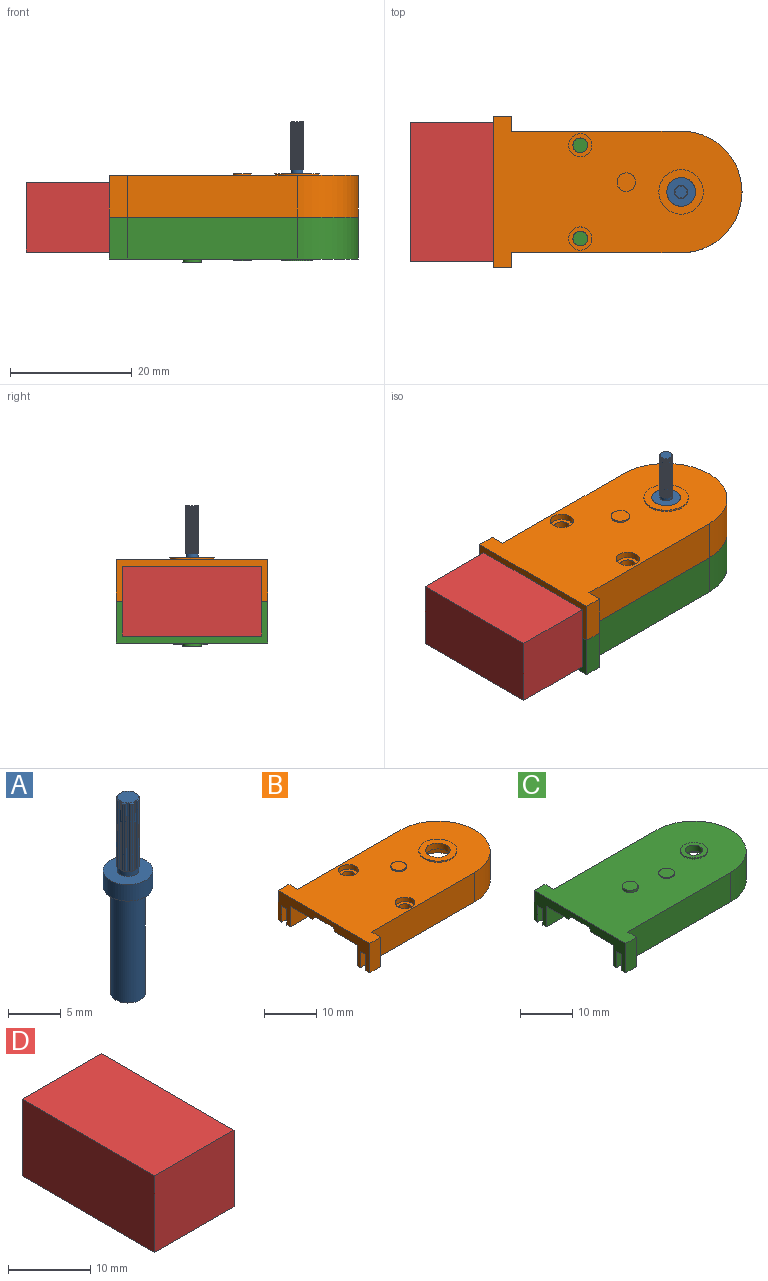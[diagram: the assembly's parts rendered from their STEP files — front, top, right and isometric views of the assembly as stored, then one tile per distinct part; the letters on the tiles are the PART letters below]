
ASSEMBLY  parts=4 mates=3
PART A: 79 faces, bbox 4.7x4.7x22.7 mm
  f0: plane 4.7x4.7mm, normal (0,0,-1), area 8.8mm2, adj f76,f77
  f1: plane 0.48x0.29mm, normal (0,0,-1), area 0mm2, adj f21,f22,f23,f24,f73
  f2: plane 0.48x0.29mm, normal (0,0,-1), area 0mm2, adj f25,f26,f27,f28,f73
  f3: plane 0.48x0.29mm, normal (0,0,-1), area 0mm2, adj f29,f30,f31,f32,f73
  f4: plane 0.48x0.29mm, normal (0,0,-1), area 0mm2, adj f33,f34,f35,f36,f73
  f5: plane 0.48x0.29mm, normal (0,0,-1), area 0mm2, adj f37,f38,f39,f40,f73
  f6: plane 0.48x0.29mm, normal (0,0,-1), area 0mm2, adj f41,f42,f43,f44,f73
  f7: plane 0.48x0.29mm, normal (0,0,-1), area 0mm2, adj f45,f46,f47,f48,f73
  f8: plane 0.48x0.29mm, normal (0,0,-1), area 0mm2, adj f17,f18,f19,f20,f73
  f9: plane 7.87x0.13mm, normal (0.71,0.71,0), area 1.5mm2, adj f17,f48,f49,f74
  f10: plane 7.87x0.19mm, normal (1,0,0), area 1.5mm2, adj f20,f21,f49,f66
  f11: plane 7.87x0.13mm, normal (0.71,-0.71,0), area 1.5mm2, adj f24,f25,f49,f67
  f12: plane 7.87x0.19mm, normal (0,-1,0), area 1.5mm2, adj f28,f29,f49,f68
  f13: plane 7.87x0.13mm, normal (-0.71,-0.71,0), area 1.5mm2, adj f32,f33,f49,f69
  f14: plane 7.87x0.19mm, normal (-1,0,0), area 1.5mm2, adj f36,f37,f49,f70
  f15: plane 7.87x0.13mm, normal (-0.71,0.71,0), area 1.5mm2, adj f40,f41,f49,f71
  f16: plane 7.87x0.19mm, normal (0,1,0), area 1.5mm2, adj f44,f45,f49,f72
  f17: plane 7.87x0.19mm, normal (-0.07,1,0), area 1.5mm2, adj f8,f9,f18,f49,f57,f74
  f18: plane 7.75x0.19mm, normal (0.88,0.47,0), area 1.7mm2, adj f8,f17,f19,f57
  f19: plane 7.75x0.21mm, normal (0.96,0.29,0), area 1.7mm2, adj f8,f18,f20,f56
  f20: plane 7.87x0.14mm, normal (0.65,-0.76,0), area 1.5mm2, adj f8,f10,f19,f49,f56,f66
  f21: plane 7.87x0.14mm, normal (0.65,0.76,0), area 1.5mm2, adj f1,f10,f22,f49,f59,f66
  f22: plane 7.75x0.21mm, normal (0.96,-0.29,0), area 1.7mm2, adj f1,f21,f23,f59
  f23: plane 7.75x0.19mm, normal (0.88,-0.47,0), area 1.7mm2, adj f1,f22,f24,f58
  f24: plane 7.87x0.19mm, normal (-0.07,-1,0), area 1.5mm2, adj f1,f11,f23,f49,f58,f67
  f25: plane 7.87x0.19mm, normal (1,0.07,0), area 1.5mm2, adj f2,f11,f26,f49,f61,f67
  f26: plane 7.75x0.19mm, normal (0.47,-0.88,0), area 1.7mm2, adj f2,f25,f27,f61
  f27: plane 7.75x0.21mm, normal (0.29,-0.96,0), area 1.7mm2, adj f2,f26,f28,f60
  f28: plane 7.87x0.14mm, normal (-0.76,-0.65,0), area 1.5mm2, adj f2,f12,f27,f49,f60,f68
  f29: plane 7.87x0.14mm, normal (0.76,-0.65,0), area 1.5mm2, adj f3,f12,f30,f49,f63,f68
  f30: plane 7.75x0.21mm, normal (-0.29,-0.96,0), area 1.7mm2, adj f3,f29,f31,f63
  f31: plane 7.75x0.19mm, normal (-0.47,-0.88,0), area 1.7mm2, adj f3,f30,f32,f62
  f32: plane 7.87x0.19mm, normal (-1,0.07,0), area 1.5mm2, adj f3,f13,f31,f49,f62,f69
  f33: plane 7.87x0.19mm, normal (0.07,-1,0), area 1.5mm2, adj f4,f13,f34,f49,f64,f69
  f34: plane 7.75x0.19mm, normal (-0.88,-0.47,0), area 1.7mm2, adj f4,f33,f35,f64
  f35: plane 7.75x0.21mm, normal (-0.96,-0.29,0), area 1.7mm2, adj f4,f34,f36,f65
  f36: plane 7.87x0.14mm, normal (-0.65,0.76,0), area 1.5mm2, adj f4,f14,f35,f49,f65,f70
  f37: plane 7.87x0.14mm, normal (-0.65,-0.76,0), area 1.5mm2, adj f5,f14,f38,f49,f51,f70
  f38: plane 7.75x0.21mm, normal (-0.96,0.29,0), area 1.7mm2, adj f5,f37,f39,f51
  f39: plane 7.75x0.19mm, normal (-0.88,0.47,0), area 1.7mm2, adj f5,f38,f40,f50
  f40: plane 7.87x0.19mm, normal (0.07,1,0), area 1.5mm2, adj f5,f15,f39,f49,f50,f71
  f41: plane 7.87x0.19mm, normal (-1,-0.07,0), area 1.5mm2, adj f6,f15,f42,f49,f53,f71
  f42: plane 7.75x0.19mm, normal (-0.47,0.88,0), area 1.7mm2, adj f6,f41,f43,f53
  f43: plane 7.75x0.21mm, normal (-0.29,0.96,0), area 1.7mm2, adj f6,f42,f44,f52
  f44: plane 7.87x0.14mm, normal (0.76,0.65,0), area 1.5mm2, adj f6,f16,f43,f49,f52,f72
  f45: plane 7.87x0.14mm, normal (-0.76,0.65,0), area 1.5mm2, adj f7,f16,f46,f49,f55,f72
  f46: plane 7.75x0.21mm, normal (0.29,0.96,0), area 1.7mm2, adj f7,f45,f47,f55
  f47: plane 7.75x0.19mm, normal (0.47,0.88,0), area 1.7mm2, adj f7,f46,f48,f54
  f48: plane 7.87x0.19mm, normal (1,-0.07,0), area 1.5mm2, adj f7,f9,f47,f49,f54,f74
  f49: plane 1.98x1.98mm, normal (0,0,1), area 3mm2, adj f9,f10,f11,f12,f13,f14,f15,f16
  f50: plane 0.24x0.24mm, normal (-0.62,0.33,0.71), area 0mm2, adj f39,f40,f49,f51
  f51: plane 0.3x0.18mm, normal (-0.68,0.21,0.71), area 0mm2, adj f37,f38,f49,f50
  f52: plane 0.3x0.18mm, normal (-0.21,0.68,0.71), area 0mm2, adj f43,f44,f49,f53
  f53: plane 0.24x0.24mm, normal (-0.33,0.62,0.71), area 0mm2, adj f41,f42,f49,f52
  f54: plane 0.24x0.24mm, normal (0.33,0.62,0.71), area 0mm2, adj f47,f48,f49,f55
  f55: plane 0.3x0.18mm, normal (0.21,0.68,0.71), area 0mm2, adj f45,f46,f49,f54
  f56: plane 0.3x0.18mm, normal (0.68,0.21,0.71), area 0mm2, adj f19,f20,f49,f57
  f57: plane 0.24x0.24mm, normal (0.62,0.33,0.71), area 0mm2, adj f17,f18,f49,f56
  f58: plane 0.24x0.24mm, normal (0.62,-0.33,0.71), area 0mm2, adj f23,f24,f49,f59
  f59: plane 0.3x0.18mm, normal (0.68,-0.21,0.71), area 0mm2, adj f21,f22,f49,f58
  f60: plane 0.3x0.18mm, normal (0.21,-0.68,0.71), area 0mm2, adj f27,f28,f49,f61
  f61: plane 0.24x0.24mm, normal (0.33,-0.62,0.71), area 0mm2, adj f25,f26,f49,f60
  f62: plane 0.24x0.24mm, normal (-0.33,-0.62,0.71), area 0mm2, adj f31,f32,f49,f63
  f63: plane 0.3x0.18mm, normal (-0.21,-0.68,0.71), area 0mm2, adj f29,f30,f49,f62
  f64: plane 0.24x0.24mm, normal (-0.62,-0.33,0.71), area 0mm2, adj f33,f34,f49,f65
  f65: plane 0.3x0.18mm, normal (-0.68,-0.21,0.71), area 0mm2, adj f35,f36,f49,f64
  f66: plane 0.28x0.06mm, normal (0,0,1), area 0mm2, adj f10,f20,f21,f73
  f67: plane 0.2x0.2mm, normal (0,0,1), area 0mm2, adj f11,f24,f25,f73
  f68: plane 0.28x0.06mm, normal (0,0,1), area 0mm2, adj f12,f28,f29,f73
  f69: plane 0.2x0.2mm, normal (0,0,1), area 0mm2, adj f13,f32,f33,f73
  f70: plane 0.28x0.06mm, normal (0,0,1), area 0mm2, adj f14,f36,f37,f73
  f71: plane 0.2x0.2mm, normal (0,0,1), area 0mm2, adj f15,f40,f41,f73
  f72: plane 0.28x0.06mm, normal (0,0,1), area 0mm2, adj f16,f44,f45,f73
  f73: cylinder r=1.01mm len=2.03mm, axis (0,0,1), area 4mm2, adj f1,f2,f3,f4,f5,f6,f7,f8
  f74: plane 0.2x0.2mm, normal (0,0,1), area 0mm2, adj f9,f17,f48,f73
  f75: plane 4.7x4.7mm, normal (0,0,1), area 14.1mm2, adj f73,f76
  f76: cylinder r=2.35mm len=4.7mm, axis (0,0,1), area 28.1mm2, adj f0,f75
  f77: cylinder r=1.65mm len=12.32mm, axis (0,0,1), area 127.8mm2, adj f0,f78
  f78: plane 3.3x3.3mm, normal (0,0,-1), area 8.6mm2, adj f77
PART B: 55 faces, bbox 40.8x24.8x7.1 mm
  f0: plane 40.82x24.79mm, normal (0,0,1), area 714.8mm2, adj f13,f14,f15,f16,f17,f18,f19,f20
  f1: cylinder r=1.21mm len=5.79mm, axis (0,0,1), area 43.9mm2, adj f2,f54
  f2: plane 40.82x19.96mm, normal (0,0,-1), area 109.5mm2, adj f1,f3,f4,f6,f7,f15,f16,f17
  f3: plane 14.92x5.74mm, normal (0,1,0), area 85.7mm2, adj f2,f5,f47,f52
  f4: cylinder r=1.21mm len=5.79mm, axis (0,0,1), area 43.9mm2, adj f2,f50
  f5: plane 32.86x18.27mm, normal (0,0,-1), area 520.8mm2, adj f3,f6,f7,f8,f45,f46,f47,f49
  f6: plane 5.74x5.63mm, normal (0,-1,0), area 32.3mm2, adj f2,f5,f45,f49
  f7: plane 14.97x5.74mm, normal (0,-1,0), area 86mm2, adj f2,f5,f47,f49
  f8: cylinder r=2.35mm len=4.7mm, axis (0,0,1), area 20.2mm2, adj f5,f22
  f9: plane 6.07x6.05mm, normal (0,0,-1), area 7.3mm2, adj f10,f20,f31,f32,f36,f37,f41,f43
  f10: plane 0.99x0.91mm, normal (1,0,0), area 0.7mm2, adj f9,f41,f42,f43
  f11: plane 2.97x1.04mm, normal (0,0,-1), area 3.1mm2, adj f13,f14,f20,f27
  f12: plane 2.97x1.04mm, normal (0,0,-1), area 3.1mm2, adj f18,f19,f20,f25
  f13: plane 6.86x2.97mm, normal (0,-1,0), area 20.4mm2, adj f0,f11,f14,f20
  f14: plane 6.86x2.41mm, normal (1,0,0), area 11.3mm2, adj f0,f11,f13,f15,f27,f28
  f15: plane 30.84x6.86mm, normal (0,-1,0), area 202.4mm2, adj f0,f2,f14,f16,f20,f28
  f16: cylinder r=9.98mm len=19.96mm, axis (0,0,-1), area 215.1mm2, adj f0,f2,f15,f17
  f17: plane 30.84x6.86mm, normal (0,1,0), area 202.4mm2, adj f0,f2,f16,f18,f20,f26
  f18: plane 6.86x2.41mm, normal (1,0,0), area 11.3mm2, adj f0,f12,f17,f19,f25,f26
  f19: plane 6.86x2.97mm, normal (0,1,0), area 20.4mm2, adj f0,f12,f18,f20
  f20: plane 24.79x6.86mm, normal (-1,0,0), area 66.7mm2, adj f0,f2,f9,f11,f12,f13,f15,f17
  f21: cylinder r=3.64mm len=7.29mm, axis (0,0,-1), area 5.8mm2, adj f0,f22
  f22: plane 7.29x7.29mm, normal (0,0,1), area 24.4mm2, adj f8,f21
  f23: cylinder r=1.51mm len=3.02mm, axis (0,0,-1), area 2.4mm2, adj f0,f24
  f24: plane 3.02x3.02mm, normal (0,0,1), area 7.2mm2, adj f23
  f25: plane 3.81x2.97mm, normal (0,-1,0), area 11.3mm2, adj f12,f18,f20,f26
  f26: plane 2.97x1.37mm, normal (0,0,-1), area 4.1mm2, adj f17,f18,f20,f25
  f27: plane 3.81x2.97mm, normal (0,1,0), area 11.3mm2, adj f11,f14,f20,f28
  f28: plane 2.97x1.37mm, normal (0,0,-1), area 4.1mm2, adj f14,f15,f20,f27
  f29: plane 6.07x5.74mm, normal (0,-1,0), area 34.3mm2, adj f2,f20,f30,f32,f33,f35
  f30: plane 6.07x6.05mm, normal (0,0,-1), area 7.3mm2, adj f20,f29,f32,f33,f34,f39,f40,f44
  f31: plane 6.07x5.74mm, normal (0,1,0), area 34.3mm2, adj f2,f9,f20,f32,f37,f38
  f32: plane 18.19x5.74mm, normal (-1,0,0), area 94.3mm2, adj f2,f9,f29,f30,f31,f34,f35,f36
  f33: plane 4.93x0.91mm, normal (1,0,0), area 4.5mm2, adj f29,f30,f34,f35
  f34: plane 5.44x0.91mm, normal (0,1,0), area 5mm2, adj f30,f32,f33,f35
  f35: plane 5.44x4.93mm, normal (0,0,-1), area 26.8mm2, adj f29,f32,f33,f34
  f36: plane 5.44x0.91mm, normal (0,-1,0), area 5mm2, adj f9,f32,f37,f38
  f37: plane 4.93x0.91mm, normal (1,0,0), area 4.5mm2, adj f9,f31,f36,f38
  f38: plane 5.44x4.93mm, normal (0,0,-1), area 26.8mm2, adj f31,f32,f36,f37
  f39: plane 5.44x0.91mm, normal (0,-1,0), area 5mm2, adj f30,f32,f40,f42
  f40: plane 0.99x0.91mm, normal (1,0,0), area 0.7mm2, adj f30,f39,f42,f44
  f41: plane 5.44x0.91mm, normal (0,1,0), area 5mm2, adj f9,f10,f32,f42
  f42: plane 7.06x6.07mm, normal (0,0,-1), area 41.6mm2, adj f10,f20,f32,f39,f40,f41,f43,f44
  f43: plane 0.91x0.64mm, normal (0,0.87,-0.49), area 0.7mm2, adj f9,f10,f20,f42
  f44: plane 0.91x0.64mm, normal (0,-0.87,-0.49), area 0.7mm2, adj f20,f30,f40,f42
  f45: plane 18.27x5.74mm, normal (1,0,0), area 96mm2, adj f2,f5,f6,f46,f48
  f46: plane 5.74x5.63mm, normal (0,1,0), area 32.3mm2, adj f2,f5,f45,f52
  f47: cylinder r=9.14mm len=18.27mm, axis (0,0,-1), area 165mm2, adj f2,f3,f5,f7
  f48: cylinder r=2.38mm len=4.76mm, axis (-1,0,0), area 7.8mm2, adj f2,f32,f45
  f49: cylinder r=2.16mm len=5.74mm, axis (0,0,1), area 57.8mm2, adj f2,f5,f6,f7
  f50: plane 3.81x3.81mm, normal (0,0,1), area 6.8mm2, adj f4,f51
  f51: cylinder r=1.91mm len=3.81mm, axis (0,0,1), area 12.8mm2, adj f0,f50
  f52: cylinder r=2.16mm len=5.74mm, axis (0,0,1), area 57.8mm2, adj f2,f3,f5,f46
  f53: cylinder r=1.91mm len=3.81mm, axis (0,0,1), area 12.8mm2, adj f0,f54
  f54: plane 3.81x3.81mm, normal (0,0,1), area 6.8mm2, adj f1,f53
PART C: 47 faces, bbox 40.8x24.8x7.4 mm
  f0: cylinder r=1.65mm len=3.3mm, axis (0,0,1), area 14.2mm2, adj f18,f41
  f1: plane 6.07x6.05mm, normal (0,0,-1), area 7.3mm2, adj f2,f13,f27,f28,f32,f33,f37,f39
  f2: plane 0.99x0.91mm, normal (1,0,0), area 0.7mm2, adj f1,f37,f38,f39
  f3: plane 2.97x1.04mm, normal (0,0,-1), area 3.1mm2, adj f6,f7,f13,f23
  f4: plane 2.97x1.04mm, normal (0,0,-1), area 3.1mm2, adj f11,f12,f13,f21
  f5: plane 40.82x24.79mm, normal (0,0,1), area 750.9mm2, adj f6,f7,f8,f9,f10,f11,f12,f13
  f6: plane 6.86x2.97mm, normal (0,-1,0), area 20.4mm2, adj f3,f5,f7,f13
  f7: plane 6.86x2.41mm, normal (1,0,0), area 11.3mm2, adj f3,f5,f6,f8,f23,f24
  f8: plane 30.84x6.86mm, normal (0,-1,0), area 202.4mm2, adj f5,f7,f9,f13,f14,f24
  f9: cylinder r=9.98mm len=19.96mm, axis (0,0,-1), area 215.1mm2, adj f5,f8,f10,f14
  f10: plane 30.84x6.86mm, normal (0,1,0), area 202.4mm2, adj f5,f9,f11,f13,f14,f22
  f11: plane 6.86x2.41mm, normal (1,0,0), area 11.3mm2, adj f4,f5,f10,f12,f21,f22
  f12: plane 6.86x2.97mm, normal (0,1,0), area 20.4mm2, adj f4,f5,f11,f13
  f13: plane 24.79x6.86mm, normal (-1,0,0), area 66.7mm2, adj f1,f3,f4,f5,f6,f8,f10,f12
  f14: plane 40.82x19.96mm, normal (0,0,-1), area 92.2mm2, adj f8,f9,f10,f13,f25,f27,f28,f42
  f15: cylinder r=1.52mm len=3.05mm, axis (0,0,-1), area 4.9mm2, adj f5,f16
  f16: plane 3.05x3.05mm, normal (0,0,1), area 7.3mm2, adj f15
  f17: cylinder r=2.59mm len=5.18mm, axis (0,0,-1), area 4.1mm2, adj f5,f18
  f18: plane 5.18x5.18mm, normal (0,0,1), area 12.5mm2, adj f0,f17
  f19: cylinder r=1.51mm len=3.02mm, axis (0,0,-1), area 2.4mm2, adj f5,f20
  f20: plane 3.02x3.02mm, normal (0,0,1), area 7.2mm2, adj f19
  f21: plane 3.81x2.97mm, normal (0,-1,0), area 11.3mm2, adj f4,f11,f13,f22
  f22: plane 2.97x1.37mm, normal (0,0,-1), area 4.1mm2, adj f10,f11,f13,f21
  f23: plane 3.81x2.97mm, normal (0,1,0), area 11.3mm2, adj f3,f7,f13,f24
  f24: plane 2.97x1.37mm, normal (0,0,-1), area 4.1mm2, adj f7,f8,f13,f23
  f25: plane 6.07x5.74mm, normal (0,-1,0), area 34.3mm2, adj f13,f14,f26,f28,f29,f31
  f26: plane 6.07x6.05mm, normal (0,0,-1), area 7.3mm2, adj f13,f25,f28,f29,f30,f35,f36,f40
  f27: plane 6.07x5.74mm, normal (0,1,0), area 34.3mm2, adj f1,f13,f14,f28,f33,f34
  f28: plane 18.19x5.74mm, normal (-1,0,0), area 94.3mm2, adj f1,f14,f25,f26,f27,f30,f31,f32
  f29: plane 4.93x0.91mm, normal (1,0,0), area 4.5mm2, adj f25,f26,f30,f31
  f30: plane 5.44x0.91mm, normal (0,1,0), area 5mm2, adj f26,f28,f29,f31
  f31: plane 5.44x4.93mm, normal (0,0,-1), area 26.8mm2, adj f25,f28,f29,f30
  f32: plane 5.44x0.91mm, normal (0,-1,0), area 5mm2, adj f1,f28,f33,f34
  f33: plane 4.93x0.91mm, normal (1,0,0), area 4.5mm2, adj f1,f27,f32,f34
  f34: plane 5.44x4.93mm, normal (0,0,-1), area 26.8mm2, adj f27,f28,f32,f33
  f35: plane 5.44x0.91mm, normal (0,-1,0), area 5mm2, adj f26,f28,f36,f38
  f36: plane 0.99x0.91mm, normal (1,0,0), area 0.7mm2, adj f26,f35,f38,f40
  f37: plane 5.44x0.91mm, normal (0,1,0), area 5mm2, adj f1,f2,f28,f38
  f38: plane 7.06x6.07mm, normal (0,0,-1), area 41.6mm2, adj f2,f13,f28,f35,f36,f37,f39,f40
  f39: plane 0.91x0.64mm, normal (0,0.87,-0.49), area 0.7mm2, adj f1,f2,f13,f38
  f40: plane 0.91x0.64mm, normal (0,-0.87,-0.49), area 0.7mm2, adj f13,f26,f36,f38
  f41: plane 32.86x18.27mm, normal (0,0,-1), area 556mm2, adj f0,f42,f43,f44,f45
  f42: plane 23.72x5.74mm, normal (0,-1,0), area 136.2mm2, adj f14,f41,f43,f45
  f43: plane 18.27x5.74mm, normal (1,0,0), area 96mm2, adj f14,f41,f42,f44,f46
  f44: plane 23.67x5.74mm, normal (0,1,0), area 135.9mm2, adj f14,f41,f43,f45
  f45: cylinder r=9.14mm len=18.27mm, axis (0,0,-1), area 165mm2, adj f14,f41,f42,f44
  f46: cylinder r=2.38mm len=4.76mm, axis (-1,0,0), area 7.8mm2, adj f14,f28,f43
PART D: 6 faces, bbox 13.6x22.9x11.4 mm
  f0: plane 22.86x11.43mm, normal (1,0,0), area 261.3mm2, adj f1,f3,f4,f5
  f1: plane 13.61x11.43mm, normal (0,1,0), area 155.6mm2, adj f0,f2,f4,f5
  f2: plane 22.86x11.43mm, normal (-1,0,0), area 261.3mm2, adj f1,f3,f4,f5
  f3: plane 13.61x11.43mm, normal (0,-1,0), area 155.6mm2, adj f0,f2,f4,f5
  f4: plane 22.86x13.61mm, normal (0,0,1), area 311.1mm2, adj f0,f1,f2,f3
  f5: plane 22.86x13.61mm, normal (0,0,-1), area 311.1mm2, adj f0,f1,f2,f3
PLACE A t=(30.84,0,7.75)mm
PLACE B at identity
PLACE C rot(axis=(1,0,0),180deg) t=(0,0,0)mm
PLACE D t=(-6.81,0,-5.71)mm
MATE fastened A.f73 <-> B.f8  axis (0,0,1) through (30.84,0,7.11)mm
MATE fastened C.f12 <-> B.f13  axis (0,-1,0) through (1.49,-12.4,0)mm
MATE fastened C.f13 <-> D.f0  axis (-1,0,0) through (0,-12.4,-6.86)mm
